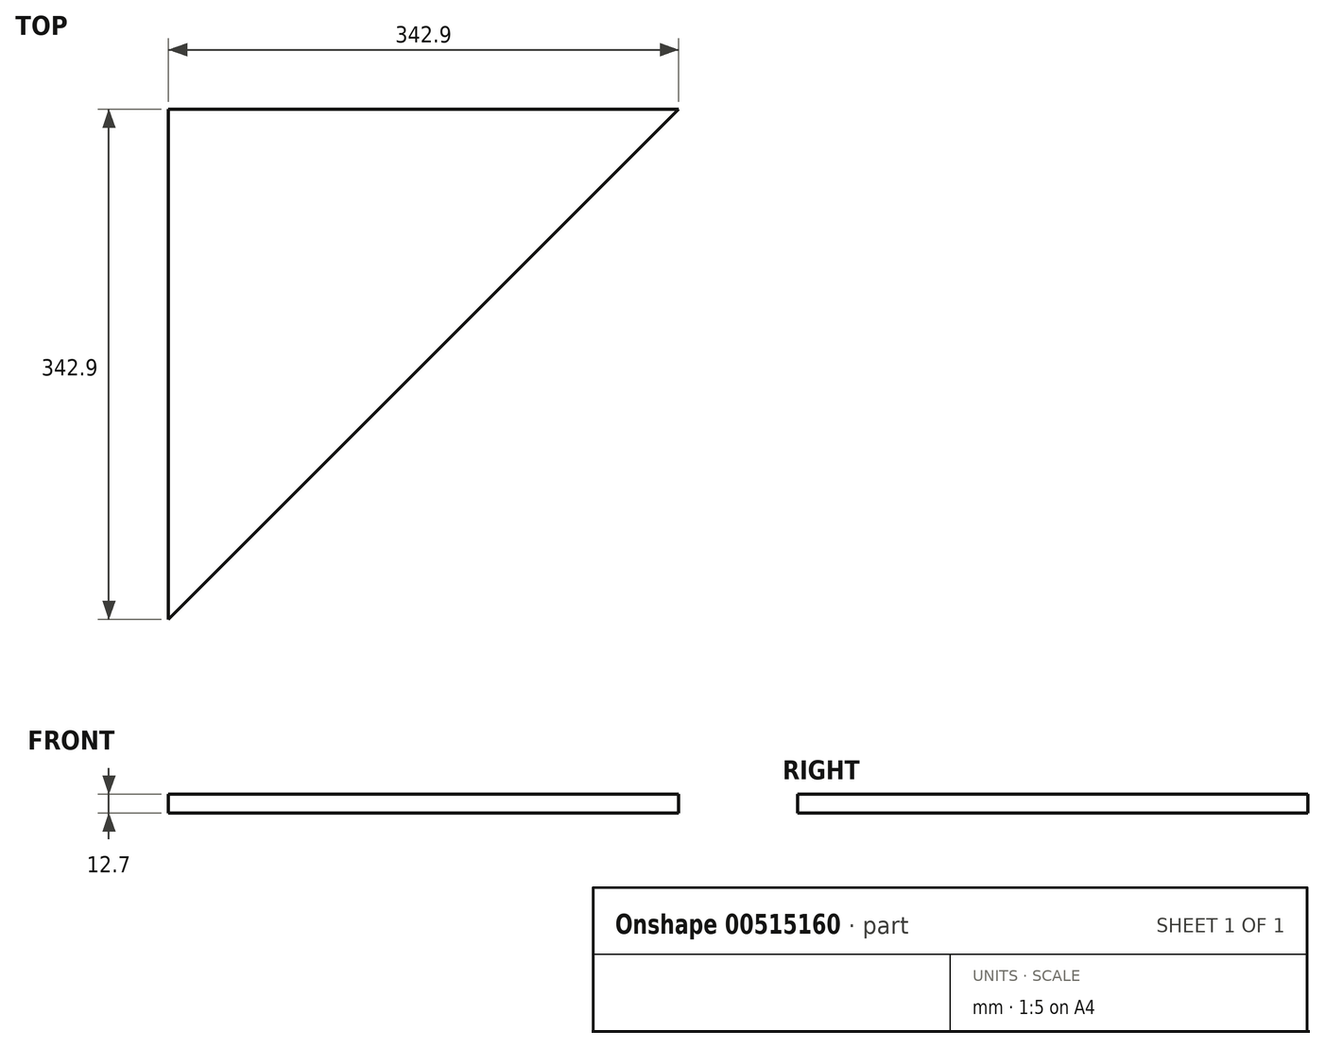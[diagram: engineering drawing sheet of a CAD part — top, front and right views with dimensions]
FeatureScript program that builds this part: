
annotation { "Feature Type Name" : "Feature", "Feature Type Description" : "" }
export const myFeature = defineFeature(function(context is Context, id is Id, definition is map)
    precondition{}
    {
        {
            var Q0;
            Q0=qCreatedBy(makeId("Top.planeOp"),FACE);
            var sketch = newSketch(context, id + "F0", { "sketchPlane" : qUnion([Q0])});
            skLineSegment(sketch, "E0", {"start": v(0, 0) * mm, "end": v(0, -342.9) * mm});
            skLineSegment(sketch, "E1", {"start": v(0, -342.9) * mm, "end": v(342.9, 0) * mm});
            skLineSegment(sketch, "E2", {"start": v(342.9, 0) * mm, "end": v(0, 0) * mm});
            skSolve(sketch);
        }
        {
            var Q0;
            Q0=makeQuery(id+"F0.imprint","IMPRINT",FACE,{"disambiguationData":[TD([[makeQuery(id+"F0.imprint","IMPRINT",EDGE,{"derivedFrom":sQuery(id+"F0.wireOp",EDGE,"E0")}),1.0]])]});
            extrude(context, id + "F1", {"entities" : qUnion([Q0]), "depth" : 12.7 * mm, "offsetDistance" : 25.4 * mm});
        }
    });
